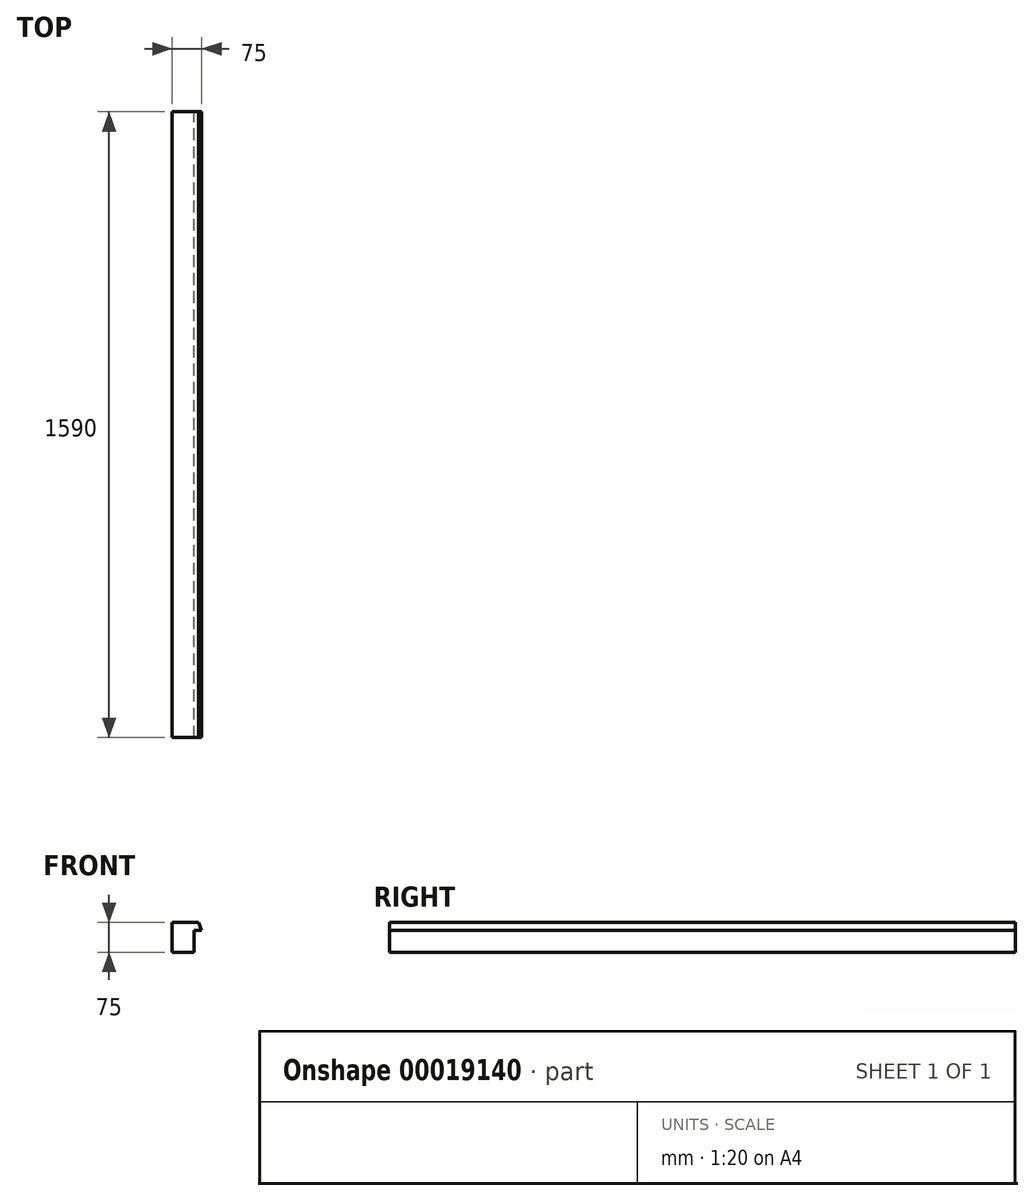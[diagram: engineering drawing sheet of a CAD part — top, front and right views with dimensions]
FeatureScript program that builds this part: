
annotation { "Feature Type Name" : "Feature", "Feature Type Description" : "" }
export const myFeature = defineFeature(function(context is Context, id is Id, definition is map)
    precondition{}
    {
        {
            var Q0;
            Q0=qCreatedBy(makeId("Front.planeOp"),FACE);
            var sketch = newSketch(context, id + "F0", { "sketchPlane" : qUnion([Q0])});
            skLineSegment(sketch, "E0.rect.bottom", {"start": v(-92.15, -5.75) * mm, "end": v(-147.15, -5.75) * mm});
            skLineSegment(sketch, "E0.rect.top", {"start": v(-80.15, 69.25) * mm, "end": v(-147.15, 69.25) * mm});
            skLineSegment(sketch, "E0.rect.right", {"start": v(-147.15, -5.75) * mm, "end": v(-147.15, 69.25) * mm});
            skPoint(sketch, "E0.rect.middle", {"position": v(-109.65, 31.75) * mm});
            skLineSegment(sketch, "E1", {"start": v(-92.15, -5.75) * mm, "end": v(-92.15, 49.25) * mm});
            skLineSegment(sketch, "E2", {"start": v(-92.15, 49.25) * mm, "end": v(-72.15, 49.25) * mm});
            skLineSegment(sketch, "E3", {"start": v(-72.15, 49.25) * mm, "end": v(-80.15, 69.25) * mm});
            skPoint(sketch, "E4.orphan", {"position": v(-72.15, 69.25) * mm});
            skPoint(sketch, "E5.orphan", {"position": v(-72.15, -5.75) * mm});
            skSolve(sketch);
        }
        {
            var Q0;
            Q0=makeQuery(id+"F0.imprint","IMPRINT",FACE,{"disambiguationData":[TD([[makeQuery(id+"F0.imprint","IMPRINT",EDGE,{"derivedFrom":sQuery(id+"F0.wireOp",EDGE,"E0.rect.bottom")}),-1.0]])]});
            extrude(context, id + "F1", {"entities" : qUnion([Q0]), "depth" : 1590 * mm});
        }
    });
